# Revit family: Walls_Finishes_EMAC_NOVOTRI-ECLIPSE-ALU-2500mm-a11-h27mm___
name_source: partatom
category: Generic Models
revit_build: Autodesk Revit 2015 (Build: 20140903_1530(x64)
units: mm (PartAtom-declared; Revit-internal decimal feet)

## types (3) — shared parameters
Edition number = 1
Manufacturer = EMAC
Product Guid = 7be11691-79af-49ad-aa9b-e1e2098bc603
Product data url = https://www.bimobject.com

## per-type parameters (varying)
| type | BLR | Description | Height | PL | Product Material | Width |
| NLECAL1125PL | No | NOVOTRI ECLIPSE ALU a:11 h:25mm PL-13 | 25 mm  [stored 0.082021 ft] | Yes | Finish_Emac_Aluminum-Anodized-Matt-Silver-13 | 11 mm  [stored 0.0360892 ft] |
| NLECAL1125BLR | Yes | NOVOTRI ECLIPSE ALU a: 27  h:11mm BL ROTO-142 | 11 mm  [stored 0.0360892 ft] | No | Finish_Emac_Aluminum-Off-White-142 | 27 mm  [stored 0.0885827 ft] |
| NLECAL1125NM | Yes | NOVOTRI ECLIPSE ALU a: 27  h:11mm NM-90 | 11 mm  [stored 0.0360892 ft] | No | Finish_Emac_Aluminum-Anodized-Matt-Black-90 | 27 mm  [stored 0.0885827 ft] |

note: [stored X ft] marks values corroborated as IEEE doubles in the binary element streams (Revit-internal decimal feet)

## geometry (parser evidence)
native form markers: Sweep x2
no freeform markers — native parametric forms only
